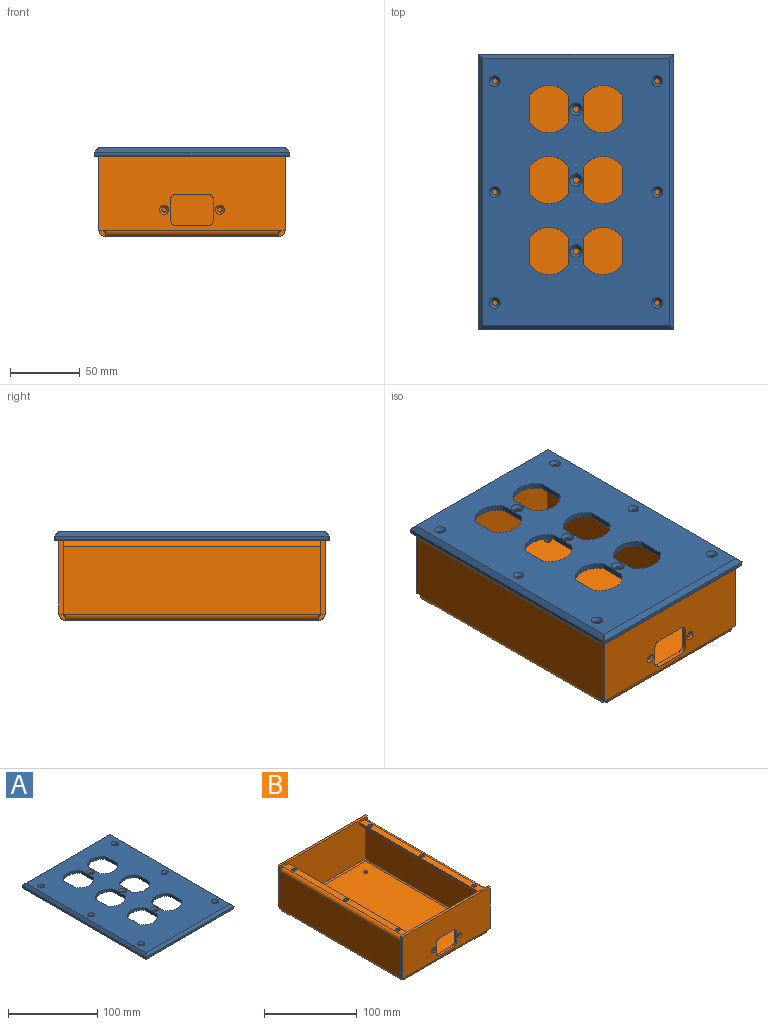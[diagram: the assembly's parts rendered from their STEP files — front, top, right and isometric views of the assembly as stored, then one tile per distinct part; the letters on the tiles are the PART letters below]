
ASSEMBLY  parts=2 mates=1
PART A: 87 faces, bbox 139.7x196.9x6.4 mm
  f0: plane 190.5x133.35mm, normal (0,0,1), area 19978.3mm2, adj f26,f28,f30,f32,f34,f36,f38,f40
  f1: plane 143.21x107.7mm, normal (0,0,-1), area 10417.5mm2, adj f7,f8,f9,f10,f11,f12,f13,f14
  f2: plane 195.26x138.11mm, normal (0,0,-1), area 10600.9mm2, adj f7,f8,f9,f10,f11,f12,f13,f14
  f3: plane 196.06x2.38mm, normal (-1,0,0), area 466.9mm2, adj f70,f71,f82,f85
  f4: plane 138.91x2.38mm, normal (0,-1,0), area 330.8mm2, adj f68,f72,f76,f85
  f5: plane 196.06x2.38mm, normal (1,0,0), area 466.9mm2, adj f67,f74,f76,f79
  f6: plane 138.91x2.38mm, normal (0,1,0), area 330.8mm2, adj f69,f73,f79,f82
  f7: plane 136.86x2.36mm, normal (1,0,0), area 323.3mm2, adj f1,f2,f8,f14
  f8: cylinder r=3.17mm len=3.18mm, axis (0,0,-1), area 11.8mm2, adj f1,f2,f7,f9
  f9: plane 101.35x2.36mm, normal (0,-1,0), area 239.4mm2, adj f1,f2,f8,f10
  f10: cylinder r=3.17mm len=3.18mm, axis (0,0,-1), area 11.8mm2, adj f1,f2,f9,f11
  f11: plane 136.86x2.36mm, normal (-1,0,0), area 323.3mm2, adj f1,f2,f10,f12
  f12: cylinder r=3.17mm len=3.18mm, axis (0,0,-1), area 11.8mm2, adj f1,f2,f11,f13
  f13: plane 101.35x2.36mm, normal (0,1,0), area 239.4mm2, adj f1,f2,f12,f14
  f14: cylinder r=3.17mm len=3.18mm, axis (0,0,-1), area 11.8mm2, adj f1,f2,f7,f13
  f15: plane 133.6x3.18mm, normal (0,1,0), area 424.2mm2, adj f2,f16,f18,f19
  f16: cylinder r=1.63mm len=3.25mm, axis (0,0,-1), area 16.2mm2, adj f2,f15,f17,f19
  f17: plane 133.6x3.18mm, normal (0,-1,0), area 424.2mm2, adj f2,f16,f18,f19
  f18: cylinder r=1.63mm len=3.25mm, axis (0,0,-1), area 16.2mm2, adj f2,f15,f17,f19
  f19: plane 136.86x3.25mm, normal (0,0,-1), area 442.7mm2, adj f15,f16,f17,f18
  f20: plane 133.6x3.18mm, normal (0,1,0), area 424.2mm2, adj f2,f21,f23,f24
  f21: cylinder r=1.63mm len=3.25mm, axis (0,0,-1), area 16.2mm2, adj f2,f20,f22,f24
  f22: plane 133.6x3.18mm, normal (0,-1,0), area 424.2mm2, adj f2,f21,f23,f24
  f23: cylinder r=1.63mm len=3.25mm, axis (0,0,-1), area 16.2mm2, adj f2,f20,f22,f24
  f24: plane 136.86x3.25mm, normal (0,0,-1), area 442.7mm2, adj f20,f21,f22,f23
  f25: cylinder r=1.9mm len=4.05mm, axis (0,0,1), area 48.3mm2, adj f2,f26
  f26: cone r=1.9mm half-angle=41deg, axis (0,0,1), area 55.5mm2, adj f0,f25
  f27: cylinder r=1.9mm len=4.05mm, axis (0,0,1), area 48.3mm2, adj f2,f28
  f28: cone r=1.9mm half-angle=41deg, axis (0,0,1), area 55.5mm2, adj f0,f27
  f29: cylinder r=1.9mm len=4.05mm, axis (0,0,1), area 48.3mm2, adj f2,f30
  f30: cone r=1.9mm half-angle=41deg, axis (0,0,1), area 55.5mm2, adj f0,f29
  f31: cylinder r=1.9mm len=4.05mm, axis (0,0,1), area 48.3mm2, adj f2,f32
  f32: cone r=1.9mm half-angle=41deg, axis (0,0,1), area 55.5mm2, adj f0,f31
  f33: cylinder r=1.9mm len=4.05mm, axis (0,0,1), area 48.3mm2, adj f2,f34
  f34: cone r=1.9mm half-angle=41deg, axis (0,0,1), area 55.5mm2, adj f0,f33
  f35: cylinder r=1.9mm len=4.05mm, axis (0,0,1), area 48.3mm2, adj f2,f36
  f36: cone r=1.9mm half-angle=41deg, axis (0,0,1), area 55.5mm2, adj f0,f35
  f37: cylinder r=2.25mm len=4.5mm, axis (0,0,1), area 24.8mm2, adj f1,f38
  f38: cone r=2.25mm half-angle=45deg, axis (0,0,1), area 66.8mm2, adj f0,f37
  f39: cylinder r=2.25mm len=4.5mm, axis (0,0,1), area 24.8mm2, adj f1,f40
  f40: cone r=2.25mm half-angle=45deg, axis (0,0,1), area 66.8mm2, adj f0,f39
  f41: cylinder r=2.25mm len=4.5mm, axis (0,0,1), area 24.8mm2, adj f1,f42
  f42: cone r=2.25mm half-angle=45deg, axis (0,0,1), area 66.8mm2, adj f0,f41
  f43: plane 18.69x3.99mm, normal (-1,0,0), area 74.5mm2, adj f0,f1,f44,f46
  f44: cylinder r=16.89mm len=28.14mm, axis (0,0,1), area 132.6mm2, adj f0,f1,f43,f45
  f45: plane 18.69x3.99mm, normal (1,0,0), area 74.5mm2, adj f0,f1,f44,f46
  f46: cylinder r=16.89mm len=28.14mm, axis (0,0,1), area 132.6mm2, adj f0,f1,f43,f45
  f47: plane 18.69x3.99mm, normal (1,0,0), area 74.5mm2, adj f0,f1,f48,f50
  f48: cylinder r=16.89mm len=28.14mm, axis (0,0,1), area 132.6mm2, adj f0,f1,f47,f49
  f49: plane 18.69x3.99mm, normal (-1,0,0), area 74.5mm2, adj f0,f1,f48,f50
  f50: cylinder r=16.89mm len=28.14mm, axis (0,0,1), area 132.6mm2, adj f0,f1,f47,f49
  f51: plane 18.69x3.99mm, normal (1,0,0), area 74.5mm2, adj f0,f1,f52,f54
  f52: cylinder r=16.89mm len=28.14mm, axis (0,0,1), area 132.6mm2, adj f0,f1,f51,f53
  f53: plane 18.69x3.99mm, normal (-1,0,0), area 74.5mm2, adj f0,f1,f52,f54
  f54: cylinder r=16.89mm len=28.14mm, axis (0,0,1), area 132.6mm2, adj f0,f1,f51,f53
  f55: plane 18.69x3.99mm, normal (1,0,0), area 74.5mm2, adj f0,f1,f56,f58
  f56: cylinder r=16.89mm len=28.14mm, axis (0,0,1), area 132.6mm2, adj f0,f1,f55,f57
  f57: plane 18.69x3.99mm, normal (-1,0,0), area 74.5mm2, adj f0,f1,f56,f58
  f58: cylinder r=16.89mm len=28.14mm, axis (0,0,1), area 132.6mm2, adj f0,f1,f55,f57
  f59: plane 18.69x3.99mm, normal (1,0,0), area 74.5mm2, adj f0,f1,f60,f62
  f60: cylinder r=16.89mm len=28.14mm, axis (0,0,1), area 132.6mm2, adj f0,f1,f59,f61
  f61: plane 18.69x3.99mm, normal (-1,0,0), area 74.5mm2, adj f0,f1,f60,f62
  f62: cylinder r=16.89mm len=28.14mm, axis (0,0,1), area 132.6mm2, adj f0,f1,f59,f61
  f63: plane 18.69x3.99mm, normal (1,0,0), area 74.5mm2, adj f0,f1,f64,f66
  f64: cylinder r=16.89mm len=28.14mm, axis (0,0,1), area 132.6mm2, adj f0,f1,f63,f65
  f65: plane 18.69x3.99mm, normal (-1,0,0), area 74.5mm2, adj f0,f1,f64,f66
  f66: cylinder r=16.89mm len=28.14mm, axis (0,0,1), area 132.6mm2, adj f0,f1,f63,f65
  f67: plane 196.27x3.18mm, normal (0.71,0,0.71), area 867.1mm2, adj f0,f5,f75,f76,f78,f79
  f68: plane 139.12x3.18mm, normal (0,-0.71,0.71), area 610.5mm2, adj f0,f4,f75,f76,f84,f85
  f69: plane 139.12x3.18mm, normal (0,0.71,0.71), area 610.5mm2, adj f0,f6,f78,f79,f81,f82
  f70: plane 196.27x3.18mm, normal (-0.71,0,0.71), area 867.1mm2, adj f0,f3,f81,f82,f84,f85
  f71: cylinder r=0.79mm len=196.06mm, axis (0,-1,0), area 244.1mm2, adj f2,f3,f83,f86
  f72: cylinder r=0.79mm len=138.91mm, axis (1,0,0), area 172.8mm2, adj f2,f4,f77,f86
  f73: cylinder r=0.79mm len=138.91mm, axis (-1,0,0), area 172.8mm2, adj f2,f6,f80,f83
  f74: cylinder r=0.79mm len=196.06mm, axis (0,1,0), area 244.1mm2, adj f2,f5,f77,f80
  f75: cylinder r=0.4mm len=3.46mm, axis (-0.58,0.58,0.58), area 2.3mm2, adj f0,f67,f68,f76
  f76: cylinder r=0.4mm len=2.42mm, axis (0,0,-1), area 1.5mm2, adj f4,f5,f67,f68,f75,f77
  f77: bspline ~0.95x0.79mm, area 0.5mm2, adj f72,f74,f76
  f78: cylinder r=0.4mm len=3.46mm, axis (-0.58,-0.58,0.58), area 2.3mm2, adj f0,f67,f69,f79
  f79: cylinder r=0.4mm len=2.42mm, axis (0,0,1), area 1.5mm2, adj f5,f6,f67,f69,f78,f80
  f80: bspline ~0.95x0.79mm, area 0.5mm2, adj f73,f74,f79
  f81: cylinder r=0.4mm len=3.46mm, axis (-0.58,0.58,-0.58), area 2.3mm2, adj f0,f69,f70,f82
  f82: cylinder r=0.4mm len=2.42mm, axis (0,0,-1), area 1.5mm2, adj f3,f6,f69,f70,f81,f83
  f83: bspline ~0.95x0.79mm, area 0.5mm2, adj f71,f73,f82
  f84: cylinder r=0.4mm len=3.46mm, axis (-0.58,-0.58,-0.58), area 2.3mm2, adj f0,f68,f70,f85
  f85: cylinder r=0.4mm len=2.42mm, axis (0,0,1), area 1.5mm2, adj f3,f4,f68,f70,f84,f86
  f86: bspline ~0.95x0.79mm, area 0.5mm2, adj f71,f72,f85
PART B: 88 faces, bbox 133.4x190.5x59.7 mm
  f0: plane 181.5x124.35mm, normal (0,0,-1), area 22498.3mm2, adj f13,f26,f30,f34,f84,f85,f86,f87
  f1: plane 181.5x124.35mm, normal (0,0,1), area 22498.3mm2, adj f14,f27,f31,f35,f84,f85,f86,f87
  f2: plane 4.5x3mm, normal (0,0,-1), area 13.5mm2, adj f7,f9,f10,f11
  f3: plane 52.65x3mm, normal (-1,0,0), area 158mm2, adj f4,f8,f9,f10
  f4: plane 3x2.54mm, normal (-1,0,0), area 7.6mm2, adj f3,f5,f9,f10
  f5: plane 133.35x3mm, normal (0,0,1), area 400.1mm2, adj f4,f6,f9,f10
  f6: plane 3x2.54mm, normal (1,0,0), area 7.6mm2, adj f5,f7,f9,f10
  f7: plane 52.65x3mm, normal (1,0,0), area 158mm2, adj f2,f6,f9,f10
  f8: plane 4.5x3mm, normal (0,0,-1), area 13.5mm2, adj f3,f9,f10,f12
  f9: plane 133.35x55.19mm, normal (0,1,0), area 7359.6mm2, adj f2,f3,f4,f5,f6,f7,f8,f13
  f10: plane 133.35x55.19mm, normal (0,-1,0), area 7359.6mm2, adj f2,f3,f4,f5,f6,f7,f8,f14
  f11: plane 4.5x4.5mm, normal (1,0,0), area 14.1mm2, adj f2,f13,f14,f28
  f12: plane 4.5x4.5mm, normal (-1,0,0), area 14.1mm2, adj f8,f13,f14,f32
  f13: cylinder r=4.5mm len=124.35mm, axis (1,0,0), area 879mm2, adj f0,f9,f11,f12
  f14: cylinder r=1.5mm len=124.35mm, axis (1,0,0), area 293mm2, adj f1,f10,f11,f12
  f15: plane 4.5x3mm, normal (0,0,-1), area 13.5mm2, adj f17,f22,f23,f25
  f16: plane 3x2.54mm, normal (-1,0,0), area 7.6mm2, adj f17,f21,f22,f23
  f17: plane 52.65x3mm, normal (-1,0,0), area 157.9mm2, adj f15,f16,f22,f23
  f18: plane 4.5x3mm, normal (0,0,-1), area 13.5mm2, adj f19,f22,f23,f24
  f19: plane 52.65x3mm, normal (1,0,0), area 157.9mm2, adj f18,f20,f22,f23
  f20: plane 3x2.54mm, normal (1,0,0), area 7.6mm2, adj f19,f21,f22,f23
  f21: plane 133.35x3mm, normal (0,0,1), area 400mm2, adj f16,f20,f22,f23
  f22: plane 133.35x55.19mm, normal (0,-1,0), area 6613.6mm2, adj f15,f16,f17,f18,f19,f20,f21,f26
  f23: plane 133.35x55.19mm, normal (0,1,0), area 6662.8mm2, adj f15,f16,f17,f18,f19,f20,f21,f27
  f24: plane 4.5x4.5mm, normal (1,0,0), area 14.1mm2, adj f18,f26,f27,f29
  f25: plane 4.5x4.5mm, normal (-1,0,0), area 14.1mm2, adj f15,f26,f27,f33
  f26: cylinder r=4.5mm len=124.35mm, axis (1,0,0), area 879mm2, adj f0,f22,f24,f25
  f27: cylinder r=1.5mm len=124.35mm, axis (1,0,0), area 293mm2, adj f1,f23,f24,f25
  f28: plane 4.5x4.5mm, normal (0,1,0), area 14.1mm2, adj f11,f30,f31,f53
  f29: plane 4.5x4.5mm, normal (0,-1,0), area 14.1mm2, adj f24,f30,f31,f51
  f30: cylinder r=4.5mm len=181.5mm, axis (0,1,0), area 1282.9mm2, adj f0,f28,f29,f55
  f31: cylinder r=1.5mm len=181.5mm, axis (0,1,0), area 427.6mm2, adj f1,f28,f29,f56
  f32: plane 4.5x4.5mm, normal (0,1,0), area 14.1mm2, adj f12,f34,f35,f36
  f33: plane 4.5x4.5mm, normal (0,-1,0), area 14.1mm2, adj f25,f34,f35,f38
  f34: cylinder r=4.5mm len=181.5mm, axis (0,1,0), area 1282.9mm2, adj f0,f32,f33,f40
  f35: cylinder r=1.5mm len=181.5mm, axis (0,1,0), area 427.6mm2, adj f1,f32,f33,f41
  f36: plane 3x1.47mm, normal (0,0,-1), area 4.4mm2, adj f32,f37,f40,f41
  f37: plane 48.15x3mm, normal (0,1,0), area 144.5mm2, adj f36,f40,f41,f47
  f38: plane 3x1.47mm, normal (0,0,-1), area 4.4mm2, adj f33,f39,f40,f41
  f39: plane 48.15x3mm, normal (0,-1,0), area 144.5mm2, adj f38,f40,f41,f48
  f40: plane 184.45x48.15mm, normal (-1,0,0), area 8881.2mm2, adj f34,f36,f37,f38,f39,f49
  f41: plane 184.45x48.15mm, normal (1,0,0), area 8881.2mm2, adj f35,f36,f37,f38,f39,f50
  f42: plane 184.45x3mm, normal (1,0,0), area 553.3mm2, adj f43,f44,f45,f46
  f43: plane 8.03x3mm, normal (0,1,0), area 24.1mm2, adj f42,f45,f46,f47
  f44: plane 8.03x3mm, normal (0,-1,0), area 24.1mm2, adj f42,f45,f46,f48
  f45: plane 184.45x8.03mm, normal (0,0,1), area 1426.8mm2, adj f42,f43,f44,f49,f78,f79,f80
  f46: plane 184.45x8.03mm, normal (0,0,-1), area 1426.8mm2, adj f42,f43,f44,f50,f78,f79,f80
  f47: plane 4.5x4.5mm, normal (0,1,0), area 14.1mm2, adj f37,f43,f49,f50
  f48: plane 4.5x4.5mm, normal (0,-1,0), area 14.1mm2, adj f39,f44,f49,f50
  f49: cylinder r=4.5mm len=184.45mm, axis (0,1,0), area 1303.8mm2, adj f40,f45,f47,f48
  f50: cylinder r=1.5mm len=184.45mm, axis (0,1,0), area 434.6mm2, adj f41,f46,f47,f48
  f51: plane 3x1.47mm, normal (0,0,-1), area 4.4mm2, adj f29,f52,f55,f56
  f52: plane 48.15x3mm, normal (0,-1,0), area 144.5mm2, adj f51,f55,f56,f62
  f53: plane 3x1.47mm, normal (0,0,-1), area 4.4mm2, adj f28,f54,f55,f56
  f54: plane 48.15x3mm, normal (0,1,0), area 144.5mm2, adj f53,f55,f56,f63
  f55: plane 184.45x48.15mm, normal (1,0,0), area 8881.2mm2, adj f30,f51,f52,f53,f54,f64
  f56: plane 184.45x48.15mm, normal (-1,0,0), area 8881.2mm2, adj f31,f51,f52,f53,f54,f65
  f57: plane 184.45x3mm, normal (-1,0,0), area 553.3mm2, adj f58,f59,f60,f61
  f58: plane 8.03x3mm, normal (0,-1,0), area 24.1mm2, adj f57,f60,f61,f62
  f59: plane 8.03x3mm, normal (0,1,0), area 24.1mm2, adj f57,f60,f61,f63
  f60: plane 184.45x8.03mm, normal (0,0,1), area 1426.8mm2, adj f57,f58,f59,f64,f81,f82,f83
  f61: plane 184.45x8.03mm, normal (0,0,-1), area 1426.8mm2, adj f57,f58,f59,f65,f81,f82,f83
  f62: plane 4.5x4.5mm, normal (0,-1,0), area 14.1mm2, adj f52,f58,f64,f65
  f63: plane 4.5x4.5mm, normal (0,1,0), area 14.1mm2, adj f54,f59,f64,f65
  f64: cylinder r=4.5mm len=184.45mm, axis (0,-1,0), area 1303.8mm2, adj f55,f60,f62,f63
  f65: cylinder r=1.5mm len=184.45mm, axis (0,-1,0), area 434.6mm2, adj f56,f61,f62,f63
  f66: plane 14.33x3mm, normal (1,0,0), area 43mm2, adj f22,f23,f67,f73
  f67: cylinder r=4.14mm len=4.14mm, axis (0,-1,0), area 19.5mm2, adj f22,f23,f66,f68
  f68: plane 22.45x3mm, normal (0,0,1), area 67.4mm2, adj f22,f23,f67,f69
  f69: cylinder r=4.14mm len=4.14mm, axis (0,-1,0), area 19.5mm2, adj f22,f23,f68,f70
  f70: plane 14.33x3mm, normal (-1,0,0), area 43mm2, adj f22,f23,f69,f71
  f71: cylinder r=4.14mm len=4.14mm, axis (0,-1,0), area 19.5mm2, adj f22,f23,f70,f72
  f72: plane 22.45x3mm, normal (0,0,-1), area 67.4mm2, adj f22,f23,f71,f73
  f73: cylinder r=4.14mm len=4.14mm, axis (0,-1,0), area 19.5mm2, adj f22,f23,f66,f72
  f74: cylinder r=1.63mm len=3.26mm, axis (0,-1,0), area 16.9mm2, adj f23,f75
  f75: cone r=1.63mm half-angle=50deg, axis (0,-1,0), area 32.1mm2, adj f22,f74
  f76: cylinder r=1.63mm len=3.26mm, axis (0,-1,0), area 16.9mm2, adj f23,f77
  f77: cone r=1.63mm half-angle=50deg, axis (0,-1,0), area 32.1mm2, adj f22,f76
  f78: cylinder r=2.38mm len=4.76mm, axis (0,0,1), area 44.9mm2, adj f45,f46
  f79: cylinder r=2.38mm len=4.76mm, axis (0,0,1), area 44.9mm2, adj f45,f46
  f80: cylinder r=2.38mm len=4.76mm, axis (0,0,1), area 44.9mm2, adj f45,f46
  f81: cylinder r=2.38mm len=4.76mm, axis (0,0,1), area 44.9mm2, adj f60,f61
  f82: cylinder r=2.38mm len=4.76mm, axis (0,0,1), area 44.9mm2, adj f60,f61
  f83: cylinder r=2.38mm len=4.76mm, axis (0,0,1), area 44.9mm2, adj f60,f61
  f84: cylinder r=2.38mm len=4.76mm, axis (0,0,1), area 44.9mm2, adj f0,f1
  f85: cylinder r=2.38mm len=4.76mm, axis (0,0,1), area 44.9mm2, adj f0,f1
  f86: cylinder r=2.38mm len=4.76mm, axis (0,0,1), area 44.9mm2, adj f0,f1
  f87: cylinder r=2.38mm len=4.76mm, axis (0,0,1), area 44.9mm2, adj f0,f1
PLACE A t=(-54.73,-32.98,81.82)mm
PLACE B t=(-51.56,-29.81,24.67)mm
MATE cylindrical B.f79 <-> A.f27  axis (0,0,1) through (-43.05,65.44,81.82)mm
